# Revit family: RRVCSAS
name_source: partatom
category: Generic Models
revit_build: Autodesk Revit 2018 (Build: 20190510_1515(x64)
units: mm (PartAtom-declared; Revit-internal decimal feet)

## family parameters
Always vertical = No
Can host rebar = No
Cut with Voids When Loaded = No
Part Type = Normal
Room Calculation Point = No
Round Connector Dimension = Use Diameter
Shared = Yes
Work Plane-Based = Yes

## types (2) — shared parameters
Default Elevation = 48 "
Rack Material = <By Category>
Width = 2 "

## per-type parameters (varying)
| type | Arm Type | Description | Rack Length | Slot Length |
| RRVCSAS1050 | RMVCSAS : RMVCSAS1050 | Rocket Rack Vertical Compact Support Assembly 304 1/2-13 Single 10.5 Inch Slot | 12.5 " | 10.5 " |
| RRVCSAS0650 | RMVCSAS : RRVCSAS0650 | Rocket Rack Vertical Compact Support Assembly 304 1/2-13 Single 6.5 Inch Slot | 8.5 " | 6.5 " |

note: column(s) folded — value = type name in every type: Catalog Number

## geometry (parser evidence)
native form markers: Sweep x12
no freeform markers — native parametric forms only
